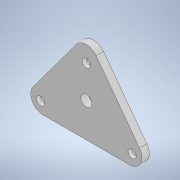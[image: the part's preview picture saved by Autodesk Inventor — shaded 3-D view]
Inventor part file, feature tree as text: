
AUTODESK INVENTOR PART (.ipt)
format: ipt  version: 2022 (Build 260153000, 153)  size: 125,440 bytes
history: native  units: mm
features: hole x2, sketch x1, extrude x1, fillet x1
ambient origin geometry x8: Origin, YZ Plane, XZ Plane, XY Plane, X Axis, Y Axis, Z Axis, Center Point
bodies: Solid1 (feature_tree)
feature tree (5):
  sketch  "Sketch1"  dims[d0=37.302465mm d1=22.623745mm d2=10.0mm d3=10.0mm d4=3.0mm d5=0.0mm d6=3.4mm d7=6.0mm d8=6.3mm d9=2.0mm d10=90.0deg d11=7.0mm d12=20.594885mm d13=4.5mm d14=6.0mm d15=9.4mm d16=2.0mm d17=90.0deg d18=7.0mm d19=20.594885mm d20=5.0mm d21=4.658158mm d22=4.658158mm]
  extrude  "Extrusion1"  Depth=5.0mm
  hole  "Hole1"  [1 undecoded]
  hole  "Hole2"  [1 undecoded]
  fillet  "Fillet1"  Radius=3.0mm
note: 2 required parameter values undecoded (feature->parameter linkage not recoverable at this tier; creation-order binding heuristic only, values carry confidence <= 0.55)
